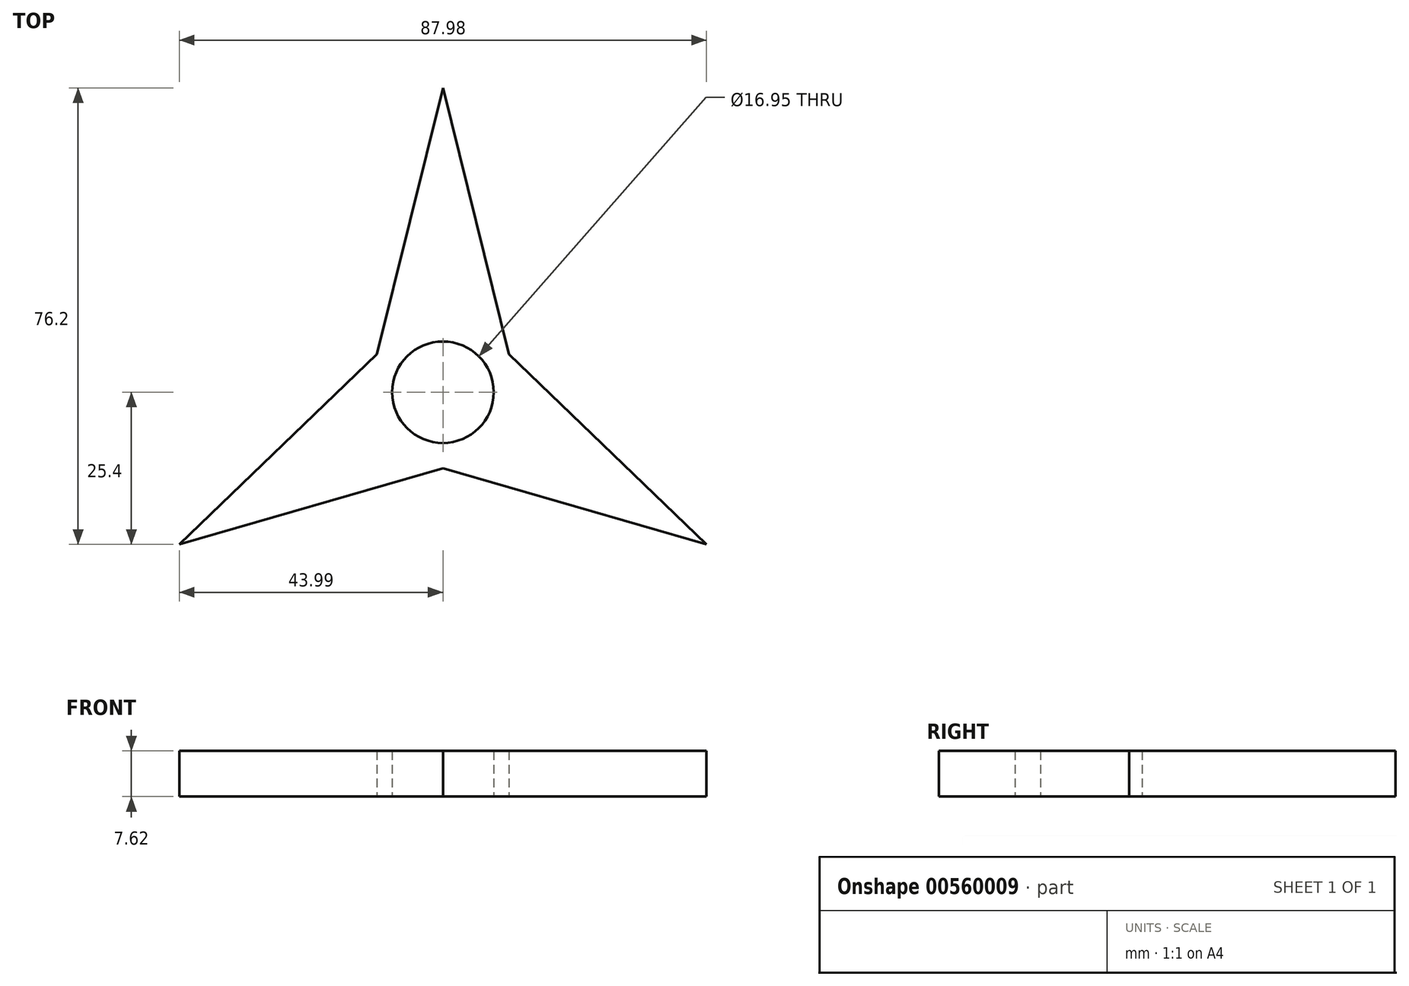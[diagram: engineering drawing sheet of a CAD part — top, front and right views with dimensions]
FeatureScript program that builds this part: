
annotation { "Feature Type Name" : "Feature", "Feature Type Description" : "" }
export const myFeature = defineFeature(function(context is Context, id is Id, definition is map)
    precondition{}
    {
        {
            var Q0;
            Q0=qCreatedBy(makeId("Top.planeOp"),FACE);
            var sketch = newSketch(context, id + "F0", { "sketchPlane" : qUnion([Q0])});
            skCircle(sketch, "E0.cCircle", {"center": v(0, 0) * mm, "radius": 25.4 * mm, "construction": true});
            skLineSegment(sketch, "E0.0", {"start": v(-44, -25.4) * mm, "end": v(0, 50.8) * mm});
            skLineSegment(sketch, "E0.1", {"start": v(0, 50.8) * mm, "end": v(44, -25.4) * mm});
            skLineSegment(sketch, "E0.2", {"start": v(44, -25.4) * mm, "end": v(-44, -25.4) * mm});
            skPoint(sketch, "E0.0.midPoint", {"position": v(-22, 12.7) * mm});
            skLineSegment(sketch, "E1", {"start": v(0, 0) * mm, "end": v(0, 50.8) * mm});
            skLineSegment(sketch, "E2", {"start": v(0, 0) * mm, "end": v(44, -25.4) * mm});
            skLineSegment(sketch, "E3", {"start": v(0, 0) * mm, "end": v(-44, -25.4) * mm});
            skLineSegment(sketch, "E4", {"start": v(0, 0) * mm, "end": v(-22, 12.7) * mm});
            skLineSegment(sketch, "E5", {"start": v(0, 0) * mm, "end": v(0, -25.4) * mm});
            skLineSegment(sketch, "E6", {"start": v(0, -25.4) * mm, "end": v(0, 0) * mm});
            skLineSegment(sketch, "E7", {"start": v(0, 0) * mm, "end": v(22, 12.7) * mm});
            skPoint(sketch, "E7.endSnap0", {"position": v(22, 12.7) * mm});
            skLineSegment(sketch, "E8", {"start": v(-44, -25.4) * mm, "end": v(-11, 6.35) * mm});
            skLineSegment(sketch, "E9", {"start": v(-11, 6.35) * mm, "end": v(0, 50.8) * mm});
            skLineSegment(sketch, "E10", {"start": v(0, 50.8) * mm, "end": v(11, 6.35) * mm});
            skLineSegment(sketch, "E11", {"start": v(11, 6.35) * mm, "end": v(44, -25.4) * mm});
            skLineSegment(sketch, "E12", {"start": v(0, -12.7) * mm, "end": v(44, -25.4) * mm});
            skLineSegment(sketch, "E13", {"start": v(0, -12.7) * mm, "end": v(-44, -25.4) * mm});
            skSolve(sketch);
        }
        {
            var Q0;
            Q0=qCreatedBy(makeId("Top.planeOp"),FACE);
            var sketch = newSketch(context, id + "F1", { "sketchPlane" : qUnion([Q0])});
            skCircle(sketch, "E14", {"center": v(0, 0) * mm, "radius": 8.48 * mm});
            skSolve(sketch);
        }
        {
            var Q0;
            {var subQ0=sQuery(id+"F0.wireOp",EDGE,"E1");Q0=makeQuery(id+"F0.imprint","IMPRINT",FACE,{"disambiguationData":[TD([[makeQuery(id+"F0.imprint","IMPRINT",EDGE,{"derivedFrom":subQ0}),1.0]])]});}
            var Q1;
            {var subQ0=sQuery(id+"F0.wireOp",EDGE,"E3");Q1=makeQuery(id+"F0.imprint","IMPRINT",FACE,{"disambiguationData":[TD([[makeQuery(id+"F0.imprint","IMPRINT",EDGE,{"derivedFrom":subQ0}),-1.0]])]});}
            var Q2;
            {var subQ0=sQuery(id+"F0.wireOp",EDGE,"E3");Q2=makeQuery(id+"F0.imprint","IMPRINT",FACE,{"disambiguationData":[TD([[makeQuery(id+"F0.imprint","IMPRINT",EDGE,{"derivedFrom":subQ0}),1.0]])]});}
            var Q3;
            {var subQ0=sQuery(id+"F0.wireOp",EDGE,"E2");Q3=makeQuery(id+"F0.imprint","IMPRINT",FACE,{"disambiguationData":[TD([[makeQuery(id+"F0.imprint","IMPRINT",EDGE,{"derivedFrom":subQ0}),-1.0]])]});}
            var Q4;
            {var subQ0=sQuery(id+"F0.wireOp",EDGE,"E1");Q4=makeQuery(id+"F0.imprint","IMPRINT",FACE,{"disambiguationData":[TD([[makeQuery(id+"F0.imprint","IMPRINT",EDGE,{"derivedFrom":subQ0}),-1.0]])]});}
            var Q5;
            {var subQ0=sQuery(id+"F0.wireOp",EDGE,"E2");Q5=makeQuery(id+"F0.imprint","IMPRINT",FACE,{"disambiguationData":[TD([[makeQuery(id+"F0.imprint","IMPRINT",EDGE,{"derivedFrom":subQ0}),1.0]])]});}
            extrude(context, id + "F2", {"entities" : qUnion([Q0, Q1, Q2, Q3, Q4, Q5]), "depth" : 7.62 * mm, "offsetDistance" : 25.4 * mm});
        }
        {
            var Q0;
            Q0 = qSketchRegion(id + "F1", true);
            extrude(context, id + "F3", {"entities" : qUnion([Q0]), "operationType" : NewBodyOperationType.REMOVE, "depth" : 73.9 * mm, "offsetDistance" : 25.4 * mm});
        }
    });
